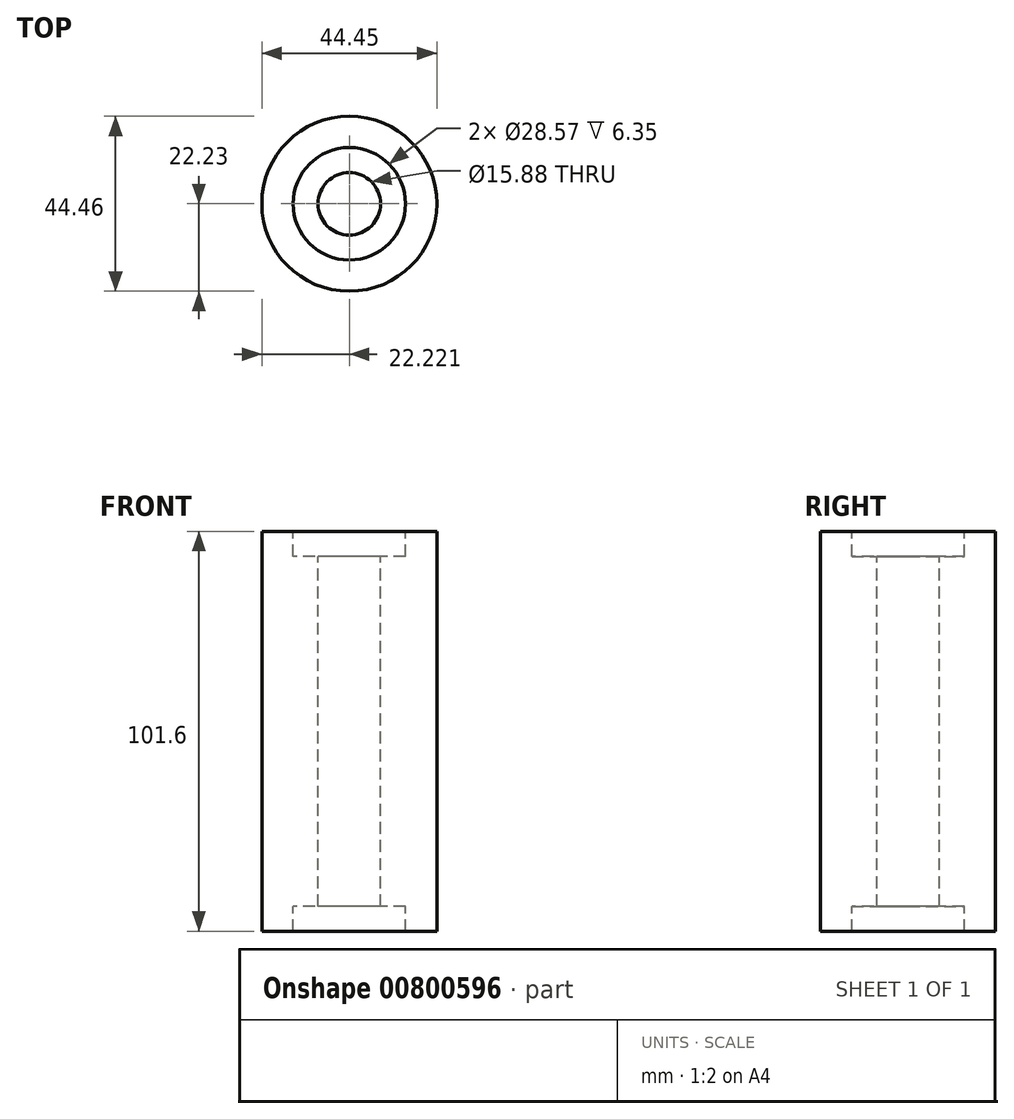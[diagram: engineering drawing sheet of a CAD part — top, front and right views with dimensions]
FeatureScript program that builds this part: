
annotation { "Feature Type Name" : "Feature", "Feature Type Description" : "" }
export const myFeature = defineFeature(function(context is Context, id is Id, definition is map)
    precondition{}
    {
        {
            var Q0;
            Q0=qCreatedBy(makeId("Front.planeOp"),FACE);
            var sketch = newSketch(context, id + "F0", { "sketchPlane" : qUnion([Q0])});
            skLineSegment(sketch, "E0", {"start": v(-78.3, 201.5) * mm, "end": v(-78.3, -80.43) * mm, "construction": true});
            skLineSegment(sketch, "E1", {"start": v(-86.24, 61.57) * mm, "end": v(-86.24, -27.33) * mm});
            skLineSegment(sketch, "E2", {"start": v(-86.24, 61.57) * mm, "end": v(-92.59, 61.57) * mm});
            skLineSegment(sketch, "E3", {"start": v(-86.24, -27.33) * mm, "end": v(-92.59, -27.33) * mm});
            skLineSegment(sketch, "E4", {"start": v(-92.59, -27.33) * mm, "end": v(-92.59, -33.68) * mm});
            skLineSegment(sketch, "E5", {"start": v(-92.59, 61.57) * mm, "end": v(-92.59, 67.92) * mm});
            skLineSegment(sketch, "E6", {"start": v(-92.59, 67.92) * mm, "end": v(-100.52, 67.92) * mm});
            skLineSegment(sketch, "E7", {"start": v(-92.59, -33.68) * mm, "end": v(-100.52, -33.68) * mm});
            skLineSegment(sketch, "E8", {"start": v(-100.52, -33.68) * mm, "end": v(-100.52, 67.92) * mm});
            skSolve(sketch);
        }
        {
            var Q0;
            Q0 = qSketchRegion(id + "F0", true);
            var Q1;
            Q1=sQuery(id+"F0.wireOp",EDGE,"E0");
            revolve(context, id + "F1", {"surfaceOperationType" : NewSurfaceOperationType.NEW, "entities" : qUnion([Q0]), "axis" : qUnion([Q1]), "revolveType" : RevolveType.FULL});
        }
    });
